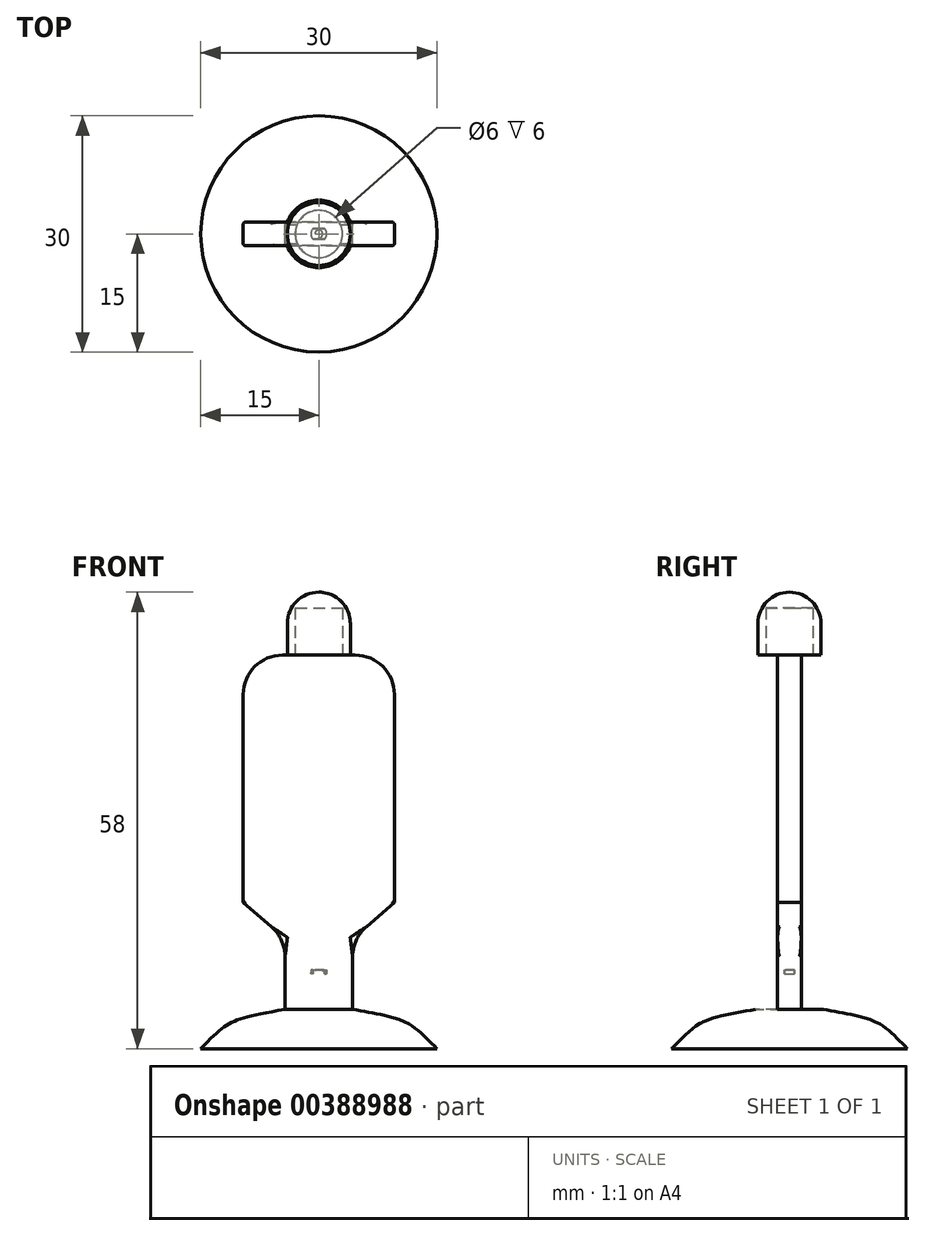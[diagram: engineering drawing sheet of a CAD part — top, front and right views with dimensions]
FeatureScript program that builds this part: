
annotation { "Feature Type Name" : "Feature", "Feature Type Description" : "" }
export const myFeature = defineFeature(function(context is Context, id is Id, definition is map)
    precondition{}
    {
        {
            var Q0;
            Q0=qCreatedBy(makeId("Front.planeOp"),FACE);
            var sketch = newSketch(context, id + "F0", { "sketchPlane" : qUnion([Q0])});
            skLineSegment(sketch, "E0", {"start": v(0, 45) * mm, "end": v(9.6, 45) * mm});
            skLineSegment(sketch, "E1", {"start": v(9.6, 45) * mm, "end": v(9.6, 13.55) * mm});
            skLineSegment(sketch, "E2", {"start": v(9.6, 13.55) * mm, "end": v(4.29, 9) * mm});
            skLineSegment(sketch, "E3", {"start": v(4.29, 9) * mm, "end": v(4.29, 0) * mm});
            skLineSegment(sketch, "E4", {"start": v(15, -5) * mm, "end": v(0, -5) * mm});
            skLineSegment(sketch, "E5", {"start": v(0, -5) * mm, "end": v(0, 45) * mm});
            skLineSegment(sketch, "E6", {"start": v(4.29, 0) * mm, "end": v(0, 0) * mm});
            skFitSpline(sketch, "E7", {"points": [v(4.29, 0) * mm, v(15, -5) * mm], "startDerivative": vector(21.1, -3.82) * mm, "endDerivative": vector(11.03, -11.18) * mm});
            skSolve(sketch);
        }
        {
            var Q0;
            {var subQ0=sQuery(id+"F0.wireOp",EDGE,"E4");Q0=makeQuery(id+"F0.imprint","IMPRINT",FACE,{"disambiguationData":[TD([[makeQuery(id+"F0.imprint","IMPRINT",EDGE,{"derivedFrom":subQ0}),-1.0]])]});}
            var Q1;
            Q1=sQuery(id+"F0.wireOp",EDGE,"E5");
            revolve(context, id + "F1", {"entities" : qUnion([Q0]), "axis" : qUnion([Q1]), "revolveType" : RevolveType.FULL});
        }
        {
            var Q0;
            Q0=makeQuery(id+"F1.opRevolve","SWEPT_FACE",FACE,{"disambiguationData":[OSD([sQuery(id+"F0.wireOp",EDGE,"E6")])]});
            var sketch = newSketch(context, id + "F2", { "sketchPlane" : qUnion([Q0])});
            skArc(sketch, "E8", {"start": v(-0.75, 0.66) * mm, "mid": v(-1, 0) * mm, "end": v(-0.75, -0.66) * mm});
            skLineSegment(sketch, "E9", {"start": v(0.75, 0.66) * mm, "end": v(-0.75, 0.66) * mm});
            skLineSegment(sketch, "E10", {"start": v(-0.75, -0.66) * mm, "end": v(0.75, -0.66) * mm});
            skArc(sketch, "E11.trimOffspring", {"start": v(0.75, -0.66) * mm, "mid": v(1, 0) * mm, "end": v(0.75, 0.66) * mm});
            skSolve(sketch);
        }
        {
            var Q0;
            Q0=makeQuery(id+"F2.imprint","IMPRINT",FACE,{"disambiguationData":[TD([[makeQuery(id+"F2.imprint","IMPRINT",EDGE,{"derivedFrom":sQuery(id+"F2.wireOp",EDGE,"E8")}),1.0]])]});
            extrude(context, id + "F3", {"entities" : qUnion([Q0]), "operationType" : NewBodyOperationType.ADD, "depth" : 5 * mm});
        }
        {
            var Q0;
            {var subQ0=sQuery(id+"F0.wireOp",EDGE,"E0");Q0=makeQuery(id+"F0.imprint","IMPRINT",FACE,{"disambiguationData":[TD([[makeQuery(id+"F0.imprint","IMPRINT",EDGE,{"derivedFrom":subQ0}),-1.0]])]});}
            extrude(context, id + "F4", {"entities" : qUnion([Q0]), "endBound" : BoundingType.SYMMETRIC, "depth" : 3 * mm});
        }
        {
            var Q0;
            Q0=makeQuery(id+"F1.opRevolve","SWEPT_BODY",BODY,{"disambiguationData":[OSD([sQuery(id+"F0.wireOp",EDGE,"E4"),sQuery(id+"F0.wireOp",EDGE,"E5"),sQuery(id+"F0.wireOp",EDGE,"E6"),sQuery(id+"F0.wireOp",EDGE,"E7")])]});
            var Q1;
            Q1=makeQuery(id+"F4.opExtrude","SWEPT_BODY",BODY,{"disambiguationData":[OSD([sQuery(id+"F0.wireOp",EDGE,"E0"),sQuery(id+"F0.wireOp",EDGE,"E1"),sQuery(id+"F0.wireOp",EDGE,"E2"),sQuery(id+"F0.wireOp",EDGE,"E3"),sQuery(id+"F0.wireOp",EDGE,"E5"),sQuery(id+"F0.wireOp",EDGE,"E6")])]});
            booleanBodies(context, id + "F5", {"operationType" : BooleanOperationType.SUBTRACTION, "tools" : qUnion([Q0]), "targets" : qUnion([Q1]), "keepTools" : true});
        }
        {
            var Q0;
            Q0=makeQuery(id+"F3.opExtrude","CAP_EDGE",EDGE,{"disambiguationData":[OSD([sQuery(id+"F2.wireOp",EDGE,"E8")])],"isStart":false});
            var Q1;
            Q1=makeQuery(id+"F3.opExtrude","CAP_EDGE",EDGE,{"disambiguationData":[OSD([sQuery(id+"F2.wireOp",EDGE,"E11.trimOffspring")])],"isStart":false});
            fillet(context, id + "F6", {"entities" : qUnion([Q0, Q1]), "radius" : 0.5 * mm, "tangentPropagation" : true, "allowEdgeOverflow" : false});
        }
        {
            var Q0;
            Q0=makeQuery(id+"F1.opRevolve","SWEPT_EDGE",EDGE,{"disambiguationData":[OSD([sQuery(id+"F0.wireOp",EDGE,"FsoU3qRD-UX4x-9X75-hpFR-DDBcEkhgQDSD"),sQuery(id+"F0.wireOp",EDGE,"4MlYxIiC-deK8-Ddmc-ACIX-NH0YoJXoCFJz")])]});
            var Q1;
            Q1=makeQuery(id+"F4.opExtrude","CAP_EDGE",EDGE,{"disambiguationData":[OSD([sQuery(id+"F0.wireOp",EDGE,"E3")])],"isStart":true});
            var Q2;
            Q2=makeQuery(id+"F4.opExtrude","CAP_EDGE",EDGE,{"disambiguationData":[OSD([sQuery(id+"F0.wireOp",EDGE,"E2")])],"isStart":true});
            var Q3;
            Q3=makeQuery(id+"F4.opExtrude","CAP_EDGE",EDGE,{"disambiguationData":[OSD([sQuery(id+"F0.wireOp",EDGE,"E1")])],"isStart":true});
            var Q4;
            Q4=makeQuery(id+"F4.opExtrude","CAP_EDGE",EDGE,{"disambiguationData":[OSD([sQuery(id+"F0.wireOp",EDGE,"E0")])],"isStart":true});
            var Q5;
            Q5=makeQuery(id+"F4.opExtrude","CAP_EDGE",EDGE,{"disambiguationData":[OSD([sQuery(id+"F0.wireOp",EDGE,"E3")])],"isStart":false});
            var Q6;
            Q6=makeQuery(id+"F4.opExtrude","CAP_EDGE",EDGE,{"disambiguationData":[OSD([sQuery(id+"F0.wireOp",EDGE,"E2")])],"isStart":false});
            var Q7;
            Q7=makeQuery(id+"F4.opExtrude","CAP_EDGE",EDGE,{"disambiguationData":[OSD([sQuery(id+"F0.wireOp",EDGE,"E1")])],"isStart":false});
            var Q8;
            Q8=makeQuery(id+"F4.opExtrude","CAP_EDGE",EDGE,{"disambiguationData":[OSD([sQuery(id+"F0.wireOp",EDGE,"E0")])],"isStart":false});
            fillet(context, id + "F7", {"entities" : qUnion([Q0, Q1, Q2, Q3, Q4, Q5, Q6, Q7, Q8]), "radius" : 0.3 * mm, "tangentPropagation" : true, "allowEdgeOverflow" : false});
        }
        {
            var Q0;
            Q0=makeQuery(id+"F4.opExtrude","SWEPT_EDGE",EDGE,{"disambiguationData":[OSD([sQuery(id+"F0.wireOp",EDGE,"E0"),sQuery(id+"F0.wireOp",EDGE,"E1")])]});
            fillet(context, id + "F8", {"entities" : qUnion([Q0]), "radius" : 5 * mm, "tangentPropagation" : true, "allowEdgeOverflow" : false});
        }
        {
            var Q0;
            Q0=makeQuery(id+"F4.opExtrude","SWEPT_EDGE",EDGE,{"disambiguationData":[OSD([sQuery(id+"F0.wireOp",EDGE,"E2"),sQuery(id+"F0.wireOp",EDGE,"E3")])]});
            fillet(context, id + "F9", {"entities" : qUnion([Q0]), "radius" : 5 * mm, "tangentPropagation" : true, "allowEdgeOverflow" : false});
        }
        {
            var Q0;
            Q0=makeQuery(id+"F4.opExtrude","SWEPT_BODY",BODY,{"disambiguationData":[OSD([sQuery(id+"F0.wireOp",EDGE,"E0"),sQuery(id+"F0.wireOp",EDGE,"E1"),sQuery(id+"F0.wireOp",EDGE,"E2"),sQuery(id+"F0.wireOp",EDGE,"E3"),sQuery(id+"F0.wireOp",EDGE,"E5"),sQuery(id+"F0.wireOp",EDGE,"E6")])]});
            var Q1;
            Q1=makeQuery(id+"F4.opExtrude","SWEPT_FACE",FACE,{"disambiguationData":[OSD([sQuery(id+"F0.wireOp",EDGE,"E5")])]});
            mirror(context, id + "F10", {"operationType" : NewBodyOperationType.ADD, "entities" : qUnion([Q0]), "mirrorPlane" : qUnion([Q1])});
        }
        {
            var Q0;
            {var subQ0=makeQuery(id+"F4.opExtrude","SWEPT_FACE",FACE,{"disambiguationData":[OSD([sQuery(id+"F0.wireOp",EDGE,"E0")])]});Q0=makeQuery(id+"FokOdn53Jpja9rY_1.boolean.opBoolean","MERGE",FACE,{"derivedFrom":[subQ0,makeQuery(id+"FokOdn53Jpja9rY_1.opPattern","COPY",FACE,{"derivedFrom":subQ0,"instanceName":"1"})]});}
            var sketch = newSketch(context, id + "F11", { "sketchPlane" : qUnion([Q0])});
            skCircle(sketch, "E12", {"center": v(0, 0) * mm, "radius": 4 * mm});
            skSolve(sketch);
        }
        {
            var Q0;
            Q0=makeQuery(id+"F11.imprint","IMPRINT",FACE,{"disambiguationData":[TD([[makeQuery(id+"F11.imprint","IMPRINT",EDGE,{"derivedFrom":sQuery(id+"F11.wireOp",EDGE,"2PEuXC6g-LR6S-ziLI-Fweo-AfXJc0oV9ggq")}),-1.0]])]});
            var Q1;
            {var subQ0=sQuery(id+"F11.wireOp",EDGE,"E12");var subQ1=sQuery(id+"F0.wireOp",EDGE,"E0");var subQ2=makeQuery(id+"F7.opFillet","BLEND_EDGE",EDGE,{"blendedFrom":[makeQuery(id+"F4.opExtrude","CAP_EDGE",EDGE,{"disambiguationData":[OSD([subQ1])],"isStart":true}),makeQuery(id+"F4.opExtrude","SWEPT_FACE",FACE,{"disambiguationData":[OSD([subQ1])]})],"blendedInto":[makeQuery(id+"F4.opExtrude","SWEPT_FACE",FACE,{"disambiguationData":[OSD([subQ1])]})]});var subQ3=makeQuery(id+"F10.boolean.opBoolean","MERGE",EDGE,{"derivedFrom":[subQ2,makeQuery(id+"F10.opPattern","COPY",EDGE,{"derivedFrom":subQ2,"instanceName":"1"})]});var subQ4=makeQuery(id+"F11.imprint","INTERSECT",VERTEX,{"disambiguationData":[OD(0.0)],"derivedFrom":[subQ3,subQ0]});Q1=makeQuery(id+"F11.imprint","IMPRINT",FACE,{"disambiguationData":[TD([[makeQuery(id+"F11.imprint","IMPRINT",EDGE,{"disambiguationData":[TD([[subQ4,1.0]])],"derivedFrom":subQ0}),1.0]])]});}
            var Q2;
            {var subQ0=sQuery(id+"F11.wireOp",EDGE,"E12");var subQ1=sQuery(id+"F0.wireOp",EDGE,"E0");var subQ2=makeQuery(id+"F7.opFillet","BLEND_EDGE",EDGE,{"blendedFrom":[makeQuery(id+"F4.opExtrude","CAP_EDGE",EDGE,{"disambiguationData":[OSD([subQ1])],"isStart":false}),makeQuery(id+"F4.opExtrude","SWEPT_FACE",FACE,{"disambiguationData":[OSD([subQ1])]})],"blendedInto":[makeQuery(id+"F4.opExtrude","SWEPT_FACE",FACE,{"disambiguationData":[OSD([subQ1])]})]});var subQ3=makeQuery(id+"F10.boolean.opBoolean","MERGE",EDGE,{"derivedFrom":[subQ2,makeQuery(id+"F10.opPattern","COPY",EDGE,{"derivedFrom":subQ2,"instanceName":"1"})]});var subQ4=makeQuery(id+"F11.imprint","INTERSECT",VERTEX,{"disambiguationData":[OD(0.0)],"derivedFrom":[subQ3,subQ0]});Q2=makeQuery(id+"F11.imprint","IMPRINT",FACE,{"disambiguationData":[TD([[makeQuery(id+"F11.imprint","IMPRINT",EDGE,{"disambiguationData":[TD([[subQ4,-1.0]])],"derivedFrom":subQ0}),1.0]])]});}
            var Q3;
            Q3=makeQuery(id+"F11.imprint","IMPRINT",FACE,{"disambiguationData":[TD([[makeQuery(id+"F11.imprint","IMPRINT",EDGE,{"derivedFrom":sQuery(id+"F11.wireOp",EDGE,"2PEuXC6g-LR6S-ziLI-Fweo-AfXJc0oV9ggq")}),1.0]])]});
            var Q4;
            {var subQ0=sQuery(id+"F11.wireOp",EDGE,"E12");var subQ1=sQuery(id+"F0.wireOp",EDGE,"E0");var subQ2=makeQuery(id+"F4.opExtrude","SWEPT_FACE",FACE,{"disambiguationData":[OSD([subQ1])]});var subQ3=makeQuery(id+"F7.opFillet","BLEND_EDGE",EDGE,{"blendedFrom":[makeQuery(id+"F4.opExtrude","CAP_EDGE",EDGE,{"disambiguationData":[OSD([subQ1])],"isStart":true}),subQ2],"blendedInto":[subQ2]});var subQ4=makeQuery(id+"F10.boolean.opBoolean","MERGE",EDGE,{"derivedFrom":[subQ3,makeQuery(id+"F10.opPattern","COPY",EDGE,{"derivedFrom":subQ3,"instanceName":"1"})]});var subQ5=makeQuery(id+"F11.imprint","INTERSECT",VERTEX,{"disambiguationData":[OD(0.0)],"derivedFrom":[subQ4,subQ0]});Q4=makeQuery(id+"F11.imprint","IMPRINT",FACE,{"disambiguationData":[TD([[makeQuery(id+"F11.imprint","IMPRINT",EDGE,{"disambiguationData":[TD([[subQ5,-1.0]])],"derivedFrom":subQ0}),1.0]])]});}
            extrude(context, id + "F12", {"entities" : qUnion([Q0, Q1, Q2, Q3, Q4]), "operationType" : NewBodyOperationType.ADD, "depth" : 8 * mm});
        }
        {
            var Q0;
            Q0=makeQuery(id+"F12.opExtrude","CAP_FACE",FACE,{"disambiguationData":[OSD([sQuery(id+"F11.wireOp",EDGE,"E12")])],"isStart":true});
            var sketch = newSketch(context, id + "F13", { "sketchPlane" : qUnion([Q0])});
            skCircle(sketch, "E13", {"center": v(0, 0) * mm, "radius": 3 * mm});
            skSolve(sketch);
        }
        {
            var Q0;
            Q0=makeQuery(id+"F13.imprint","IMPRINT",FACE,{"disambiguationData":[TD([[makeQuery(id+"F13.imprint","IMPRINT",EDGE,{"derivedFrom":sQuery(id+"F13.wireOp",EDGE,"E13")}),1.0]])]});
            extrude(context, id + "F14", {"entities" : qUnion([Q0]), "operationType" : NewBodyOperationType.REMOVE, "oppositeDirection" : true, "depth" : 6 * mm});
        }
        {
            var Q0;
            Q0=makeQuery(id+"F12.opExtrude","CAP_EDGE",EDGE,{"disambiguationData":[OSD([sQuery(id+"F11.wireOp",EDGE,"E12")])],"isStart":false});
            fillet(context, id + "F15", {"entities" : qUnion([Q0]), "radius" : 4 * mm, "tangentPropagation" : true, "allowEdgeOverflow" : false});
        }
    });
